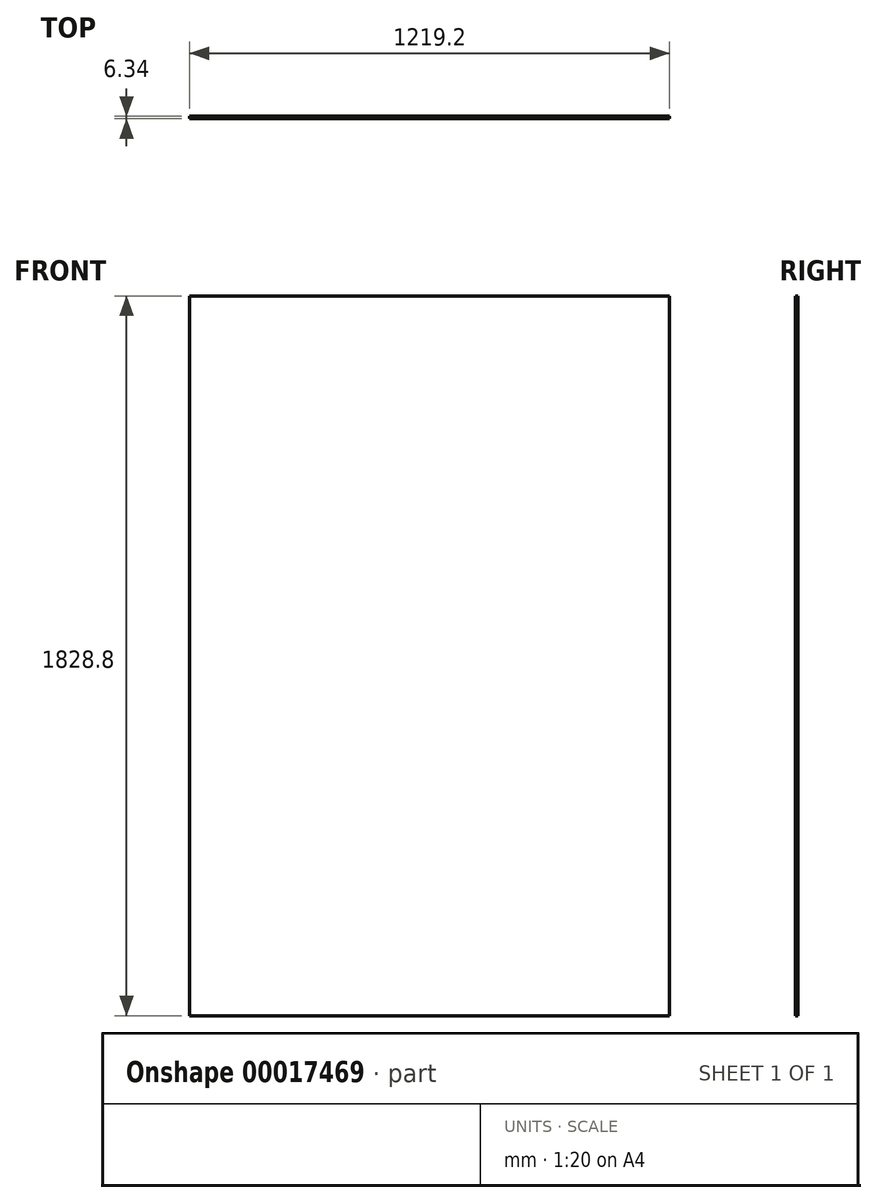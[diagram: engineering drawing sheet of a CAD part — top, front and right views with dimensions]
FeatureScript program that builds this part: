
annotation { "Feature Type Name" : "Feature", "Feature Type Description" : "" }
export const myFeature = defineFeature(function(context is Context, id is Id, definition is map)
    precondition{}
    {
        {
            var Q0;
            Q0=qCreatedBy(makeId("Front.planeOp"),FACE);
            var sketch = newSketch(context, id + "F0", { "sketchPlane" : qUnion([Q0])});
            skLineSegment(sketch, "E0.bottom", {"start": v(-609.6, 914.4) * mm, "end": v(609.6, 914.4) * mm});
            skLineSegment(sketch, "E0.top", {"start": v(-609.6, -914.4) * mm, "end": v(609.6, -914.4) * mm});
            skLineSegment(sketch, "E0.left", {"start": v(-609.6, 914.4) * mm, "end": v(-609.6, -914.4) * mm});
            skLineSegment(sketch, "E0.right", {"start": v(609.6, 914.4) * mm, "end": v(609.6, -914.4) * mm});
            skSolve(sketch);
        }
        {
            var Q0;
            Q0=makeQuery(id+"F0.imprint","IMPRINT",FACE,{"disambiguationData":[TD([[makeQuery(id+"F0.imprint","IMPRINT",EDGE,{"derivedFrom":sQuery(id+"F0.wireOp",EDGE,"E0.bottom")}),-1.0]])]});
            extrude(context, id + "F1", {"entities" : qUnion([Q0]), "endBound" : BoundingType.SYMMETRIC, "depth" : 6.35 * mm});
        }
    });
